# Revit family: 540_Sliding_Window_XX_Standard
name_source: partatom
category: Windows
revit_build: Autodesk Revit 2014 (Build: 20130308_1515(x64)
units: mm (PartAtom-declared; Revit-internal decimal feet)

## types (72) — shared parameters
Centered In Wall = Yes
Custom Sash Width Left = 600 mm  [stored 1.9685 ft]
Default Sill Height = 800 mm
Description = Sliding window, XX
Equal Sash Width = Yes
Frame Thickness = 54 mm  [stored 0.177165 ft]
Limit Sash Height Max = 1500 mm  [stored 4.92126 ft]
Limit Sash Height Min = 300 mm  [stored 0.984252 ft]
Limit Sash Width Max = 1200 mm
Limit Sash Width Min = 300 mm  [stored 0.984252 ft]
Limit Window Height Max = 1580 mm
Limit Window Height Min = 380 mm
Limit Window Width Max = 2418 mm
Limit Window Width Min = 618 mm
Manufacturer = Crealco
Model = 540
Rough Width = 3 mm  [stored 0.00984252 ft]
Sash Frame Seal = 3 mm  [stored 0.00984252 ft]
URL = http://www.crealco.co.za
Wall Closure = By host
zero-valued in all types: Custom Frame Offset From Exterior

## per-type parameters (varying)
- 540SW-0906XX-1000Pa: Area Left Sash Glazing=0.13 m²; Area Right Sash Glazing=0.13 m²; Clearvue SHGC Value=0.399; Clearvue U Value=7.2; Custom Windload=1000 mm  [stored 3.28084 ft]; Custom Window Height=590 mm  [stored 1.9357 ft]; Custom Window Width=890 mm  [stored 2.91995 ft]; Energy Advantage SHGC Value=0.632; Energy Advantage U Value=6.03; Heavy Duty Interlocker=No; Height=590 mm  [stored 1.9357 ft]; Intruderprufe LowE SHGC Value=0.339; Intruderprufe LowE U Value=6.19; Intruderprufe SHGC Value=0.378; Intruderprufe U Value=7.09; Is Heavy Duty Interlocker=0 mm  [stored 0 ft]; Limit Sash Width Left Max=572 mm; Limit Sash Width Left Min=300 mm  [stored 0.984252 ft]; Max Pane Area=0.13 m²; Sash Height=510 mm; Sash Width Left=436 mm; Sash Width Right=436 mm; Standard Interlocker=Yes; Width=890 mm  [stored 2.91995 ft]; Windload Design=1000 mm  [stored 3.28084 ft]
- 540SW-1206XX-1000Pa: Area Left Sash Glazing=0.19 m²; Area Right Sash Glazing=0.19 m²; Clearvue SHGC Value=0.44; Clearvue U Value=7.04; Custom Windload=1000 mm  [stored 3.28084 ft]; Custom Window Height=590 mm  [stored 1.9357 ft]; Custom Window Width=1190 mm  [stored 3.9042 ft]; Energy Advantage SHGC Value=0.397; Energy Advantage U Value=6.02; Heavy Duty Interlocker=No; Height=590 mm  [stored 1.9357 ft]; Intruderprufe LowE SHGC Value=0.372; Intruderprufe LowE U Value=5.692; Intruderprufe SHGC Value=0.416; Intruderprufe U Value=6.93; Is Heavy Duty Interlocker=0 mm  [stored 0 ft]; Limit Sash Width Left Max=872 mm; Limit Sash Width Left Min=300 mm  [stored 0.984252 ft]; Max Pane Area=0.19 m²; Sash Height=510 mm; Sash Width Left=586 mm; Sash Width Right=586 mm; Standard Interlocker=Yes; Width=1190 mm  [stored 3.9042 ft]; Windload Design=1000 mm  [stored 3.28084 ft]
- 540SW-1506XX-1000Pa: Area Left Sash Glazing=0.25 m²; Area Right Sash Glazing=0.25 m²; Clearvue SHGC Value=0.464; Clearvue U Value=6.94; Custom Windload=1000 mm  [stored 3.28084 ft]; Custom Window Height=590 mm  [stored 1.9357 ft]; Custom Window Width=1490 mm  [stored 4.88845 ft]; Energy Advantage SHGC Value=0.419; Energy Advantage U Value=5.85; Heavy Duty Interlocker=No; Height=590 mm  [stored 1.9357 ft]; Intruderprufe LowE SHGC Value=0.392; Intruderprufe LowE U Value=5.75; Intruderprufe SHGC Value=0.439; Intruderprufe U Value=6.83; Is Heavy Duty Interlocker=0 mm  [stored 0 ft]; Limit Sash Width Left Max=1172 mm; Limit Sash Width Left Min=300 mm  [stored 0.984252 ft]; Max Pane Area=0.25 m²; Sash Height=510 mm; Sash Width Left=736 mm; Sash Width Right=736 mm; Standard Interlocker=Yes; Width=1490 mm  [stored 4.88845 ft]; Windload Design=1000 mm  [stored 3.28084 ft]
- 540SW-1806XX-1000Pa: Area Left Sash Glazing=0.31 m²; Area Right Sash Glazing=0.31 m²; Clearvue SHGC Value=0.48; Clearvue U Value=6.88; Custom Windload=1000 mm  [stored 3.28084 ft]; Custom Window Height=590 mm  [stored 1.9357 ft]; Custom Window Width=1790 mm  [stored 5.8727 ft]; Energy Advantage SHGC Value=0.433; Energy Advantage U Value=5.74; Heavy Duty Interlocker=No; Height=590 mm  [stored 1.9357 ft]; Intruderprufe LowE SHGC Value=0.405; Intruderprufe LowE U Value=5.65; Intruderprufe SHGC Value=0.454; Intruderprufe U Value=6.77; Is Heavy Duty Interlocker=0 mm  [stored 0 ft]; Limit Sash Width Left Max=1200 mm; Limit Sash Width Left Min=572 mm; Max Pane Area=0.31 m²; Sash Height=510 mm; Sash Width Left=886 mm; Sash Width Right=886 mm; Standard Interlocker=Yes; Width=1790 mm  [stored 5.8727 ft]; Windload Design=1000 mm  [stored 3.28084 ft]
- 540SW-2106XX-1000Pa: Area Left Sash Glazing=0.37 m²; Area Right Sash Glazing=0.37 m²; Clearvue SHGC Value=0.492; Clearvue U Value=6.83; Custom Windload=1000 mm  [stored 3.28084 ft]; Custom Window Height=590 mm  [stored 1.9357 ft]; Custom Window Width=2090 mm  [stored 6.85696 ft]; Energy Advantage SHGC Value=0.443; Energy Advantage U Value=5.66; Heavy Duty Interlocker=No; Height=590 mm  [stored 1.9357 ft]; Intruderprufe LowE SHGC Value=0.414; Intruderprufe LowE U Value=5.57; Intruderprufe SHGC Value=0.465; Intruderprufe U Value=6.72; Is Heavy Duty Interlocker=0 mm  [stored 0 ft]; Limit Sash Width Left Max=1200 mm; Limit Sash Width Left Min=872 mm; Max Pane Area=0.37 m²; Sash Height=510 mm; Sash Width Left=1036 mm; Sash Width Right=1036 mm; Standard Interlocker=Yes; Width=2090 mm  [stored 6.85696 ft]; Windload Design=1000 mm  [stored 3.28084 ft]
- 540SW-2406XX-1000Pa: Area Left Sash Glazing=0.43 m²; Area Right Sash Glazing=0.43 m²; Clearvue SHGC Value=0.501; Clearvue U Value=6.8; Custom Windload=1000 mm  [stored 3.28084 ft]; Custom Window Height=590 mm  [stored 1.9357 ft]; Custom Window Width=2390 mm  [stored 7.84121 ft]; Energy Advantage SHGC Value=0.451; Energy Advantage U Value=5.61; Heavy Duty Interlocker=No; Height=590 mm  [stored 1.9357 ft]; Intruderprufe LowE SHGC Value=0.421; Intruderprufe LowE U Value=5.51; Intruderprufe SHGC Value=0.473; Intruderprufe U Value=6.69; Is Heavy Duty Interlocker=0 mm  [stored 0 ft]; Limit Sash Width Left Max=1200 mm; Limit Sash Width Left Min=1172 mm; Max Pane Area=0.43 m²; Sash Height=510 mm; Sash Width Left=1186 mm; Sash Width Right=1186 mm; Standard Interlocker=Yes; Width=2390 mm  [stored 7.84121 ft]; Windload Design=1000 mm  [stored 3.28084 ft]
- 540SW-0909XX-1000Pa: Area Left Sash Glazing=0.23 m²; Area Right Sash Glazing=0.23 m²; Clearvue SHGC Value=0.465; Clearvue U Value=7.31; Custom Windload=1000 mm  [stored 3.28084 ft]; Custom Window Height=890 mm  [stored 2.91995 ft]; Custom Window Width=890 mm  [stored 2.91995 ft]; Energy Advantage SHGC Value=0.42; Energy Advantage U Value=6.02; Heavy Duty Interlocker=No; Height=890 mm  [stored 2.91995 ft]; Intruderprufe LowE SHGC Value=0.392; Intruderprufe LowE U Value=5.91; Intruderprufe SHGC Value=0.439; Intruderprufe U Value=6.99; Is Heavy Duty Interlocker=0 mm  [stored 0 ft]; Limit Sash Width Left Max=572 mm; Limit Sash Width Left Min=300 mm  [stored 0.984252 ft]; Max Pane Area=0.23 m²; Sash Height=810 mm; Sash Width Left=436 mm; Sash Width Right=436 mm; Standard Interlocker=Yes; Width=890 mm  [stored 2.91995 ft]; Windload Design=1000 mm  [stored 3.28084 ft]
- 540SW-1209XX-1000Pa: Area Left Sash Glazing=0.34 m²; Area Right Sash Glazing=0.34 m²; Clearvue SHGC Value=0.513; Clearvue U Value=6.91; Custom Windload=1000 mm  [stored 3.28084 ft]; Custom Window Height=890 mm  [stored 2.91995 ft]; Custom Window Width=1190 mm  [stored 3.9042 ft]; Energy Advantage SHGC Value=0.462; Energy Advantage U Value=5.68; Heavy Duty Interlocker=No; Height=890 mm  [stored 2.91995 ft]; Intruderprufe LowE SHGC Value=0.432; Intruderprufe LowE U Value=5.59; Intruderprufe SHGC Value=0.485; Intruderprufe U Value=6.79; Is Heavy Duty Interlocker=0 mm  [stored 0 ft]; Limit Sash Width Left Max=872 mm; Limit Sash Width Left Min=300 mm  [stored 0.984252 ft]; Max Pane Area=0.34 m²; Sash Height=810 mm; Sash Width Left=586 mm; Sash Width Right=586 mm; Standard Interlocker=Yes; Width=1190 mm  [stored 3.9042 ft]; Windload Design=1000 mm  [stored 3.28084 ft]
- 540SW-1509XX-1000Pa: Area Left Sash Glazing=0.44 m²; Area Right Sash Glazing=0.44 m²; Clearvue SHGC Value=0.543; Clearvue U Value=6.79; Custom Windload=1000 mm  [stored 3.28084 ft]; Custom Window Height=890 mm  [stored 2.91995 ft]; Custom Window Width=1490 mm  [stored 4.88845 ft]; Energy Advantage SHGC Value=0.488; Energy Advantage U Value=5.48; Heavy Duty Interlocker=No; Height=890 mm  [stored 2.91995 ft]; Intruderprufe LowE SHGC Value=0.455; Intruderprufe LowE U Value=5.39; Intruderprufe SHGC Value=0.512; Intruderprufe U Value=6.68; Is Heavy Duty Interlocker=0 mm  [stored 0 ft]; Limit Sash Width Left Max=1172 mm; Limit Sash Width Left Min=300 mm  [stored 0.984252 ft]; Max Pane Area=0.44 m²; Sash Height=810 mm; Sash Width Left=736 mm; Sash Width Right=736 mm; Standard Interlocker=Yes; Width=1490 mm  [stored 4.88845 ft]; Windload Design=1000 mm  [stored 3.28084 ft]
- 540SW-1809XX-1000Pa: Area Left Sash Glazing=0.55 m²; Area Right Sash Glazing=0.55 m²; Clearvue SHGC Value=0.562; Clearvue U Value=6.71; Custom Windload=1000 mm  [stored 3.28084 ft]; Custom Window Height=890 mm  [stored 2.91995 ft]; Custom Window Width=1790 mm  [stored 5.8727 ft]; Energy Advantage SHGC Value=0.505; Energy Advantage U Value=5.35; Heavy Duty Interlocker=No; Height=890 mm  [stored 2.91995 ft]; Intruderprufe LowE SHGC Value=0.471; Intruderprufe LowE U Value=5.26; Intruderprufe SHGC Value=0.53; Intruderprufe U Value=6.6; Is Heavy Duty Interlocker=0 mm  [stored 0 ft]; Limit Sash Width Left Max=1200 mm; Limit Sash Width Left Min=572 mm; Max Pane Area=0.55 m²; Sash Height=810 mm; Sash Width Left=886 mm; Sash Width Right=886 mm; Standard Interlocker=Yes; Width=1790 mm  [stored 5.8727 ft]; Windload Design=1000 mm  [stored 3.28084 ft]
- 540SW-2109XX-1000Pa: Area Left Sash Glazing=0.65 m²; Area Right Sash Glazing=0.65 m²; Clearvue SHGC Value=0.576; Clearvue U Value=6.66; Custom Windload=1000 mm  [stored 3.28084 ft]; Custom Window Height=890 mm  [stored 2.91995 ft]; Custom Window Width=2090 mm  [stored 6.85696 ft]; Energy Advantage SHGC Value=0.517; Energy Advantage U Value=5.26; Heavy Duty Interlocker=No; Height=890 mm  [stored 2.91995 ft]; Intruderprufe LowE SHGC Value=0.482; Intruderprufe LowE U Value=5.16; Intruderprufe SHGC Value=0.543; Intruderprufe U Value=6.54; Is Heavy Duty Interlocker=0 mm  [stored 0 ft]; Limit Sash Width Left Max=1200 mm; Limit Sash Width Left Min=872 mm; Max Pane Area=0.65 m²; Sash Height=810 mm; Sash Width Left=1036 mm; Sash Width Right=1036 mm; Standard Interlocker=Yes; Width=2090 mm  [stored 6.85696 ft]; Windload Design=1000 mm  [stored 3.28084 ft]
- 540SW-2409XX-1000Pa: Area Left Sash Glazing=0.76 m²; Area Right Sash Glazing=0.76 m²; Clearvue SHGC Value=0.586; Clearvue U Value=6.62; Custom Windload=1000 mm  [stored 3.28084 ft]; Custom Window Height=890 mm  [stored 2.91995 ft]; Custom Window Width=2390 mm  [stored 7.84121 ft]; Energy Advantage SHGC Value=0.526; Energy Advantage U Value=5.19; Heavy Duty Interlocker=No; Height=890 mm  [stored 2.91995 ft]; Intruderprufe LowE SHGC Value=0.491; Intruderprufe LowE U Value=5.09; Intruderprufe SHGC Value=0.553; Intruderprufe U Value=6.5; Is Heavy Duty Interlocker=0 mm  [stored 0 ft]; Limit Sash Width Left Max=1200 mm; Limit Sash Width Left Min=1172 mm; Max Pane Area=0.76 m²; Sash Height=810 mm; Sash Width Left=1186 mm; Sash Width Right=1186 mm; Standard Interlocker=Yes; Width=2390 mm  [stored 7.84121 ft]; Windload Design=1000 mm  [stored 3.28084 ft]
- 540SW-0912XX-1000Pa: Area Left Sash Glazing=0.33 m²; Area Right Sash Glazing=0.33 m²; Clearvue SHGC Value=0.497; Clearvue U Value=7.29; Custom Windload=1000 mm  [stored 3.28084 ft]; Custom Window Height=1190 mm  [stored 3.9042 ft]; Custom Window Width=890 mm  [stored 2.91995 ft]; Energy Advantage SHGC Value=0.447; Energy Advantage U Value=6.02; Heavy Duty Interlocker=No; Height=1190 mm  [stored 3.9042 ft]; Intruderprufe LowE SHGC Value=0.419; Intruderprufe LowE U Value=5.92; Intruderprufe SHGC Value=0.47; Intruderprufe U Value=7.12; Is Heavy Duty Interlocker=0 mm  [stored 0 ft]; Limit Sash Width Left Max=572 mm; Limit Sash Width Left Min=300 mm  [stored 0.984252 ft]; Max Pane Area=0.33 m²; Sash Height=1110 mm; Sash Width Left=436 mm; Sash Width Right=436 mm; Standard Interlocker=Yes; Width=890 mm  [stored 2.91995 ft]; Windload Design=1000 mm  [stored 3.28084 ft]
- 540SW-1212XX-1000Pa: Area Left Sash Glazing=0.48 m²; Area Right Sash Glazing=0.48 m²; Clearvue SHGC Value=0.55; Clearvue U Value=6.84; Custom Windload=1000 mm  [stored 3.28084 ft]; Custom Window Height=1190 mm  [stored 3.9042 ft]; Custom Window Width=1190 mm  [stored 3.9042 ft]; Energy Advantage SHGC Value=0.495; Energy Advantage U Value=5.52; Heavy Duty Interlocker=No; Height=1190 mm  [stored 3.9042 ft]; Intruderprufe LowE SHGC Value=0.462; Intruderprufe LowE U Value=5.42; Intruderprufe SHGC Value=0.519; Intruderprufe U Value=6.73; Is Heavy Duty Interlocker=0 mm  [stored 0 ft]; Limit Sash Width Left Max=872 mm; Limit Sash Width Left Min=300 mm  [stored 0.984252 ft]; Max Pane Area=0.48 m²; Sash Height=1110 mm; Sash Width Left=586 mm; Sash Width Right=586 mm; Standard Interlocker=Yes; Width=1190 mm  [stored 3.9042 ft]; Windload Design=1000 mm  [stored 3.28084 ft]
- 540SW-1512XX-1000Pa: Area Left Sash Glazing=0.63 m²; Area Right Sash Glazing=0.63 m²; Clearvue SHGC Value=0.582; Clearvue U Value=6.72; Custom Windload=1000 mm  [stored 3.28084 ft]; Custom Window Height=1190 mm  [stored 3.9042 ft]; Custom Window Width=1490 mm  [stored 4.88845 ft]; Energy Advantage SHGC Value=0.522; Energy Advantage U Value=5.3; Heavy Duty Interlocker=No; Height=1190 mm  [stored 3.9042 ft]; Intruderprufe LowE SHGC Value=0.487; Intruderprufe LowE U Value=5.21; Intruderprufe SHGC Value=0.549; Intruderprufe U Value=6.6; Is Heavy Duty Interlocker=0 mm  [stored 0 ft]; Limit Sash Width Left Max=1172 mm; Limit Sash Width Left Min=300 mm  [stored 0.984252 ft]; Max Pane Area=0.63 m²; Sash Height=1110 mm; Sash Width Left=736 mm; Sash Width Right=736 mm; Standard Interlocker=Yes; Width=1490 mm  [stored 4.88845 ft]; Windload Design=1000 mm  [stored 3.28084 ft]
- 540SW-1812XX-1000Pa: Area Left Sash Glazing=0.78 m²; Area Right Sash Glazing=0.78 m²; Clearvue SHGC Value=0.602; Clearvue U Value=6.63; Custom Windload=1000 mm  [stored 3.28084 ft]; Custom Window Height=1190 mm  [stored 3.9042 ft]; Custom Window Width=1790 mm  [stored 5.8727 ft]; Energy Advantage SHGC Value=0.541; Energy Advantage U Value=5.16; Heavy Duty Interlocker=No; Height=1190 mm  [stored 3.9042 ft]; Intruderprufe LowE SHGC Value=0.504; Intruderprufe LowE U Value=5.07; Intruderprufe SHGC Value=0.568; Intruderprufe U Value=6.52; Is Heavy Duty Interlocker=0 mm  [stored 0 ft]; Limit Sash Width Left Max=1200 mm; Limit Sash Width Left Min=572 mm; Max Pane Area=0.78 m²; Sash Height=1110 mm; Sash Width Left=886 mm; Sash Width Right=886 mm; Standard Interlocker=Yes; Width=1790 mm  [stored 5.8727 ft]; Windload Design=1000 mm  [stored 3.28084 ft]
- 540SW-2112XX-1000Pa: Area Left Sash Glazing=0.93 m²; Area Right Sash Glazing=0.93 m²; Clearvue SHGC Value=0.617; Clearvue U Value=6.57; Custom Windload=1000 mm  [stored 3.28084 ft]; Custom Window Height=1190 mm  [stored 3.9042 ft]; Custom Window Width=2090 mm  [stored 6.85696 ft]; Energy Advantage SHGC Value=0.554; Energy Advantage U Value=5.05; Heavy Duty Interlocker=No; Height=1190 mm  [stored 3.9042 ft]; Intruderprufe LowE SHGC Value=0.516; Intruderprufe LowE U Value=4.96; Intruderprufe SHGC Value=0.582; Intruderprufe U Value=6.46; Is Heavy Duty Interlocker=0 mm  [stored 0 ft]; Limit Sash Width Left Max=1200 mm; Limit Sash Width Left Min=872 mm; Max Pane Area=0.93 m²; Sash Height=1110 mm; Sash Width Left=1036 mm; Sash Width Right=1036 mm; Standard Interlocker=Yes; Width=2090 mm  [stored 6.85696 ft]; Windload Design=1000 mm  [stored 3.28084 ft]
- 540SW-2412XX-1000Pa: Area Left Sash Glazing=1.08 m²; Area Right Sash Glazing=1.08 m²; Clearvue SHGC Value=0.629; Clearvue U Value=6.53; Custom Windload=1000 mm  [stored 3.28084 ft]; Custom Window Height=1190 mm  [stored 3.9042 ft]; Custom Window Width=2390 mm  [stored 7.84121 ft]; Energy Advantage SHGC Value=0.564; Energy Advantage U Value=4.98; Heavy Duty Interlocker=No; Height=1190 mm  [stored 3.9042 ft]; Intruderprufe LowE SHGC Value=0.525; Intruderprufe LowE U Value=4.89; Intruderprufe SHGC Value=0.593; Intruderprufe U Value=6.41; Is Heavy Duty Interlocker=0 mm  [stored 0 ft]; Limit Sash Width Left Max=1200 mm; Limit Sash Width Left Min=1172 mm; Max Pane Area=1.08 m²; Sash Height=1110 mm; Sash Width Left=1186 mm; Sash Width Right=1186 mm; Standard Interlocker=Yes; Width=2390 mm  [stored 7.84121 ft]; Windload Design=1000 mm  [stored 3.28084 ft]
- 540SW-0915XX-1000Pa: Area Left Sash Glazing=0.43 m²; Area Right Sash Glazing=0.43 m²; Clearvue SHGC Value=0.517; Clearvue U Value=7.27; Custom Windload=1000 mm  [stored 3.28084 ft]; Custom Window Height=1490 mm  [stored 4.88845 ft]; Custom Window Width=890 mm  [stored 2.91995 ft]; Energy Advantage SHGC Value=0.465; Energy Advantage U Value=5.94; Heavy Duty Interlocker=No; Height=1490 mm  [stored 4.88845 ft]; Intruderprufe LowE SHGC Value=0.435; Intruderprufe LowE U Value=5.84; Intruderprufe SHGC Value=0.448; Intruderprufe U Value=7.09; Is Heavy Duty Interlocker=0 mm  [stored 0 ft]; Limit Sash Width Left Max=572 mm; Limit Sash Width Left Min=300 mm  [stored 0.984252 ft]; Max Pane Area=0.43 m²; Sash Height=1410 mm; Sash Width Left=436 mm; Sash Width Right=436 mm; Standard Interlocker=Yes; Width=890 mm  [stored 2.91995 ft]; Windload Design=1000 mm  [stored 3.28084 ft]
- 540SW-1215XX-1000Pa: Area Left Sash Glazing=0.62 m²; Area Right Sash Glazing=0.62 m²; Clearvue SHGC Value=0.572; Clearvue U Value=6.8; Custom Windload=1000 mm  [stored 3.28084 ft]; Custom Window Height=1490 mm  [stored 4.88845 ft]; Custom Window Width=1190 mm  [stored 3.9042 ft]; Energy Advantage SHGC Value=0.514; Energy Advantage U Value=5.42; Heavy Duty Interlocker=No; Height=1490 mm  [stored 4.88845 ft]; Intruderprufe LowE SHGC Value=0.479; Intruderprufe LowE U Value=5.32; Intruderprufe SHGC Value=0.54; Intruderprufe U Value=6.69; Is Heavy Duty Interlocker=0 mm  [stored 0 ft]; Limit Sash Width Left Max=872 mm; Limit Sash Width Left Min=300 mm  [stored 0.984252 ft]; Max Pane Area=0.62 m²; Sash Height=1410 mm; Sash Width Left=586 mm; Sash Width Right=586 mm; Standard Interlocker=Yes; Width=1190 mm  [stored 3.9042 ft]; Windload Design=1000 mm  [stored 3.28084 ft]
- 540SW-1515XX-1000Pa: Area Left Sash Glazing=0.82 m²; Area Right Sash Glazing=0.82 m²; Clearvue SHGC Value=0.605; Clearvue U Value=6.67; Custom Windload=1000 mm  [stored 3.28084 ft]; Custom Window Height=1490 mm  [stored 4.88845 ft]; Custom Window Width=1490 mm  [stored 4.88845 ft]; Energy Advantage SHGC Value=0.543; Energy Advantage U Value=5.19; Heavy Duty Interlocker=Yes; Height=1490 mm  [stored 4.88845 ft]; Intruderprufe LowE SHGC Value=0.506; Intruderprufe LowE U Value=5.1; Intruderprufe SHGC Value=0.57; Intruderprufe U Value=6.55; Is Heavy Duty Interlocker=1 mm  [stored 0.00328084 ft]; Limit Sash Width Left Max=1172 mm; Limit Sash Width Left Min=300 mm  [stored 0.984252 ft]; Max Pane Area=0.82 m²; Sash Height=1410 mm; Sash Width Left=736 mm; Sash Width Right=736 mm; Standard Interlocker=No; Width=1490 mm  [stored 4.88845 ft]; Windload Design=1000 mm  [stored 3.28084 ft]
- 540SW-1815XX-1000Pa: Area Left Sash Glazing=1.01 m²; Area Right Sash Glazing=1.01 m²; Clearvue SHGC Value=0.627; Clearvue U Value=6.58; Custom Windload=1000 mm  [stored 3.28084 ft]; Custom Window Height=1490 mm  [stored 4.88845 ft]; Custom Window Width=1790 mm  [stored 5.8727 ft]; Energy Advantage SHGC Value=0.562; Energy Advantage U Value=5.04; Heavy Duty Interlocker=Yes; Height=1490 mm  [stored 4.88845 ft]; Intruderprufe LowE SHGC Value=0.524; Intruderprufe LowE U Value=4.95; Intruderprufe SHGC Value=0.591; Intruderprufe U Value=6.47; Is Heavy Duty Interlocker=1 mm  [stored 0.00328084 ft]; Limit Sash Width Left Max=1200 mm; Limit Sash Width Left Min=572 mm; Max Pane Area=1.01 m²; Sash Height=1410 mm; Sash Width Left=886 mm; Sash Width Right=886 mm; Standard Interlocker=No; Width=1790 mm  [stored 5.8727 ft]; Windload Design=1000 mm  [stored 3.28084 ft]
- 540SW-2115XX-1000Pa: Area Left Sash Glazing=1.21 m²; Area Right Sash Glazing=1.21 m²; Clearvue SHGC Value=0.642; Clearvue U Value=6.52; Custom Windload=1000 mm  [stored 3.28084 ft]; Custom Window Height=1490 mm  [stored 4.88845 ft]; Custom Window Width=2090 mm  [stored 6.85696 ft]; Energy Advantage SHGC Value=0.576; Energy Advantage U Value=4.93; Heavy Duty Interlocker=Yes; Height=1490 mm  [stored 4.88845 ft]; Intruderprufe LowE SHGC Value=0.536; Intruderprufe LowE U Value=4.84; Intruderprufe SHGC Value=0.606; Intruderprufe U Value=6.4; Is Heavy Duty Interlocker=1 mm  [stored 0.00328084 ft]; Limit Sash Width Left Max=1200 mm; Limit Sash Width Left Min=872 mm; Max Pane Area=1.21 m²; Sash Height=1410 mm; Sash Width Left=1036 mm; Sash Width Right=1036 mm; Standard Interlocker=No; Width=2090 mm  [stored 6.85696 ft]; Windload Design=1000 mm  [stored 3.28084 ft]
- 540SW-2415XX-1000Pa: Area Left Sash Glazing=1.4 m²; Area Right Sash Glazing=1.4 m²; Clearvue SHGC Value=0.654; Clearvue U Value=6.48; Custom Windload=1000 mm  [stored 3.28084 ft]; Custom Window Height=1490 mm  [stored 4.88845 ft]; Custom Window Width=2390 mm  [stored 7.84121 ft]; Energy Advantage SHGC Value=0.586; Energy Advantage U Value=4.85; Heavy Duty Interlocker=Yes; Height=1490 mm  [stored 4.88845 ft]; Intruderprufe LowE SHGC Value=0.546; Intruderprufe LowE U Value=4.77; Intruderprufe SHGC Value=0.617; Intruderprufe U Value=6.36; Is Heavy Duty Interlocker=1 mm  [stored 0.00328084 ft]; Limit Sash Width Left Max=1200 mm; Limit Sash Width Left Min=1172 mm; Max Pane Area=1.4 m²; Sash Height=1410 mm; Sash Width Left=1186 mm; Sash Width Right=1186 mm; Standard Interlocker=No; Width=2390 mm  [stored 7.84121 ft]; Windload Design=1000 mm  [stored 3.28084 ft]
- 540SW-0906XX-1500Pa: Area Left Sash Glazing=0.13 m²; Area Right Sash Glazing=0.13 m²; Clearvue SHGC Value=0.399; Clearvue U Value=7.2; Custom Windload=1500 mm  [stored 4.92126 ft]; Custom Window Height=590 mm  [stored 1.9357 ft]; Custom Window Width=890 mm  [stored 2.91995 ft]; Energy Advantage SHGC Value=0.632; Energy Advantage U Value=6.03; Heavy Duty Interlocker=No; Height=590 mm  [stored 1.9357 ft]; Intruderprufe LowE SHGC Value=0.339; Intruderprufe LowE U Value=6.19; Intruderprufe SHGC Value=0.378; Intruderprufe U Value=7.09; Is Heavy Duty Interlocker=0 mm  [stored 0 ft]; Limit Sash Width Left Max=572 mm; Limit Sash Width Left Min=300 mm  [stored 0.984252 ft]; Max Pane Area=0.13 m²; Sash Height=510 mm; Sash Width Left=436 mm; Sash Width Right=436 mm; Standard Interlocker=Yes; Width=890 mm  [stored 2.91995 ft]; Windload Design=1500 mm  [stored 4.92126 ft]
- 540SW-0906XX-2000Pa: Area Left Sash Glazing=0.13 m²; Area Right Sash Glazing=0.13 m²; Clearvue SHGC Value=0.399; Clearvue U Value=7.2; Custom Windload=2000 mm  [stored 6.56168 ft]; Custom Window Height=590 mm  [stored 1.9357 ft]; Custom Window Width=890 mm  [stored 2.91995 ft]; Energy Advantage SHGC Value=0.632; Energy Advantage U Value=6.03; Heavy Duty Interlocker=No; Height=590 mm  [stored 1.9357 ft]; Intruderprufe LowE SHGC Value=0.339; Intruderprufe LowE U Value=6.19; Intruderprufe SHGC Value=0.378; Intruderprufe U Value=7.09; Is Heavy Duty Interlocker=0 mm  [stored 0 ft]; Limit Sash Width Left Max=572 mm; Limit Sash Width Left Min=300 mm  [stored 0.984252 ft]; Max Pane Area=0.13 m²; Sash Height=510 mm; Sash Width Left=436 mm; Sash Width Right=436 mm; Standard Interlocker=Yes; Width=890 mm  [stored 2.91995 ft]; Windload Design=2000 mm  [stored 6.56168 ft]
- 540SW-0909XX-1500Pa: Area Left Sash Glazing=0.23 m²; Area Right Sash Glazing=0.23 m²; Clearvue SHGC Value=0.465; Clearvue U Value=7.31; Custom Windload=1500 mm  [stored 4.92126 ft]; Custom Window Height=890 mm  [stored 2.91995 ft]; Custom Window Width=890 mm  [stored 2.91995 ft]; Energy Advantage SHGC Value=0.42; Energy Advantage U Value=6.02; Heavy Duty Interlocker=No; Height=890 mm  [stored 2.91995 ft]; Intruderprufe LowE SHGC Value=0.392; Intruderprufe LowE U Value=5.91; Intruderprufe SHGC Value=0.439; Intruderprufe U Value=6.99; Is Heavy Duty Interlocker=0 mm  [stored 0 ft]; Limit Sash Width Left Max=572 mm; Limit Sash Width Left Min=300 mm  [stored 0.984252 ft]; Max Pane Area=0.23 m²; Sash Height=810 mm; Sash Width Left=436 mm; Sash Width Right=436 mm; Standard Interlocker=Yes; Width=890 mm  [stored 2.91995 ft]; Windload Design=1500 mm  [stored 4.92126 ft]
- 540SW-0909XX-2000Pa: Area Left Sash Glazing=0.23 m²; Area Right Sash Glazing=0.23 m²; Clearvue SHGC Value=0.465; Clearvue U Value=7.31; Custom Windload=2000 mm  [stored 6.56168 ft]; Custom Window Height=890 mm  [stored 2.91995 ft]; Custom Window Width=890 mm  [stored 2.91995 ft]; Energy Advantage SHGC Value=0.42; Energy Advantage U Value=6.02; Heavy Duty Interlocker=No; Height=890 mm  [stored 2.91995 ft]; Intruderprufe LowE SHGC Value=0.392; Intruderprufe LowE U Value=5.91; Intruderprufe SHGC Value=0.439; Intruderprufe U Value=6.99; Is Heavy Duty Interlocker=0 mm  [stored 0 ft]; Limit Sash Width Left Max=572 mm; Limit Sash Width Left Min=300 mm  [stored 0.984252 ft]; Max Pane Area=0.23 m²; Sash Height=810 mm; Sash Width Left=436 mm; Sash Width Right=436 mm; Standard Interlocker=Yes; Width=890 mm  [stored 2.91995 ft]; Windload Design=2000 mm  [stored 6.56168 ft]
- 540SW-0912XX-1500Pa: Area Left Sash Glazing=0.33 m²; Area Right Sash Glazing=0.33 m²; Clearvue SHGC Value=0.497; Clearvue U Value=7.29; Custom Windload=1500 mm  [stored 4.92126 ft]; Custom Window Height=1190 mm  [stored 3.9042 ft]; Custom Window Width=890 mm  [stored 2.91995 ft]; Energy Advantage SHGC Value=0.447; Energy Advantage U Value=6.02; Heavy Duty Interlocker=No; Height=1190 mm  [stored 3.9042 ft]; Intruderprufe LowE SHGC Value=0.419; Intruderprufe LowE U Value=5.92; Intruderprufe SHGC Value=0.47; Intruderprufe U Value=7.12; Is Heavy Duty Interlocker=0 mm  [stored 0 ft]; Limit Sash Width Left Max=572 mm; Limit Sash Width Left Min=300 mm  [stored 0.984252 ft]; Max Pane Area=0.33 m²; Sash Height=1110 mm; Sash Width Left=436 mm; Sash Width Right=436 mm; Standard Interlocker=Yes; Width=890 mm  [stored 2.91995 ft]; Windload Design=1500 mm  [stored 4.92126 ft]
- 540SW-0912XX-2000Pa: Area Left Sash Glazing=0.33 m²; Area Right Sash Glazing=0.33 m²; Clearvue SHGC Value=0.497; Clearvue U Value=7.29; Custom Windload=2000 mm  [stored 6.56168 ft]; Custom Window Height=1190 mm  [stored 3.9042 ft]; Custom Window Width=890 mm  [stored 2.91995 ft]; Energy Advantage SHGC Value=0.447; Energy Advantage U Value=6.02; Heavy Duty Interlocker=No; Height=1190 mm  [stored 3.9042 ft]; Intruderprufe LowE SHGC Value=0.419; Intruderprufe LowE U Value=5.92; Intruderprufe SHGC Value=0.47; Intruderprufe U Value=7.12; Is Heavy Duty Interlocker=0 mm  [stored 0 ft]; Limit Sash Width Left Max=572 mm; Limit Sash Width Left Min=300 mm  [stored 0.984252 ft]; Max Pane Area=0.33 m²; Sash Height=1110 mm; Sash Width Left=436 mm; Sash Width Right=436 mm; Standard Interlocker=Yes; Width=890 mm  [stored 2.91995 ft]; Windload Design=2000 mm  [stored 6.56168 ft]
- 540SW-0915XX-1500Pa: Area Left Sash Glazing=0.43 m²; Area Right Sash Glazing=0.43 m²; Clearvue SHGC Value=0.517; Clearvue U Value=7.27; Custom Windload=1500 mm  [stored 4.92126 ft]; Custom Window Height=1490 mm  [stored 4.88845 ft]; Custom Window Width=890 mm  [stored 2.91995 ft]; Energy Advantage SHGC Value=0.465; Energy Advantage U Value=5.94; Heavy Duty Interlocker=Yes; Height=1490 mm  [stored 4.88845 ft]; Intruderprufe LowE SHGC Value=0.435; Intruderprufe LowE U Value=5.84; Intruderprufe SHGC Value=0.448; Intruderprufe U Value=7.09; Is Heavy Duty Interlocker=1 mm  [stored 0.00328084 ft]; Limit Sash Width Left Max=572 mm; Limit Sash Width Left Min=300 mm  [stored 0.984252 ft]; Max Pane Area=0.43 m²; Sash Height=1410 mm; Sash Width Left=436 mm; Sash Width Right=436 mm; Standard Interlocker=No; Width=890 mm  [stored 2.91995 ft]; Windload Design=1500 mm  [stored 4.92126 ft]
- 540SW-0915XX-2000Pa: Area Left Sash Glazing=0.43 m²; Area Right Sash Glazing=0.43 m²; Clearvue SHGC Value=0.517; Clearvue U Value=7.27; Custom Windload=2000 mm  [stored 6.56168 ft]; Custom Window Height=1490 mm  [stored 4.88845 ft]; Custom Window Width=890 mm  [stored 2.91995 ft]; Energy Advantage SHGC Value=0.465; Energy Advantage U Value=5.94; Heavy Duty Interlocker=Yes; Height=1490 mm  [stored 4.88845 ft]; Intruderprufe LowE SHGC Value=0.435; Intruderprufe LowE U Value=5.84; Intruderprufe SHGC Value=0.448; Intruderprufe U Value=7.09; Is Heavy Duty Interlocker=1 mm  [stored 0.00328084 ft]; Limit Sash Width Left Max=572 mm; Limit Sash Width Left Min=300 mm  [stored 0.984252 ft]; Max Pane Area=0.43 m²; Sash Height=1410 mm; Sash Width Left=436 mm; Sash Width Right=436 mm; Standard Interlocker=No; Width=890 mm  [stored 2.91995 ft]; Windload Design=2000 mm  [stored 6.56168 ft]
- 540SW-1206XX-1500Pa: Area Left Sash Glazing=0.19 m²; Area Right Sash Glazing=0.19 m²; Clearvue SHGC Value=0.44; Clearvue U Value=7.04; Custom Windload=1500 mm  [stored 4.92126 ft]; Custom Window Height=590 mm  [stored 1.9357 ft]; Custom Window Width=1190 mm  [stored 3.9042 ft]; Energy Advantage SHGC Value=0.397; Energy Advantage U Value=6.02; Heavy Duty Interlocker=No; Height=590 mm  [stored 1.9357 ft]; Intruderprufe LowE SHGC Value=0.372; Intruderprufe LowE U Value=5.692; Intruderprufe SHGC Value=0.416; Intruderprufe U Value=6.93; Is Heavy Duty Interlocker=0 mm  [stored 0 ft]; Limit Sash Width Left Max=872 mm; Limit Sash Width Left Min=300 mm  [stored 0.984252 ft]; Max Pane Area=0.19 m²; Sash Height=510 mm; Sash Width Left=586 mm; Sash Width Right=586 mm; Standard Interlocker=Yes; Width=1190 mm  [stored 3.9042 ft]; Windload Design=1500 mm  [stored 4.92126 ft]
- 540SW-1206XX-2000Pa: Area Left Sash Glazing=0.19 m²; Area Right Sash Glazing=0.19 m²; Clearvue SHGC Value=0.44; Clearvue U Value=7.04; Custom Windload=2000 mm  [stored 6.56168 ft]; Custom Window Height=590 mm  [stored 1.9357 ft]; Custom Window Width=1190 mm  [stored 3.9042 ft]; Energy Advantage SHGC Value=0.397; Energy Advantage U Value=6.02; Heavy Duty Interlocker=No; Height=590 mm  [stored 1.9357 ft]; Intruderprufe LowE SHGC Value=0.372; Intruderprufe LowE U Value=5.692; Intruderprufe SHGC Value=0.416; Intruderprufe U Value=6.93; Is Heavy Duty Interlocker=0 mm  [stored 0 ft]; Limit Sash Width Left Max=872 mm; Limit Sash Width Left Min=300 mm  [stored 0.984252 ft]; Max Pane Area=0.19 m²; Sash Height=510 mm; Sash Width Left=586 mm; Sash Width Right=586 mm; Standard Interlocker=Yes; Width=1190 mm  [stored 3.9042 ft]; Windload Design=2000 mm  [stored 6.56168 ft]
- 540SW-1209XX-1500Pa: Area Left Sash Glazing=0.34 m²; Area Right Sash Glazing=0.34 m²; Clearvue SHGC Value=0.513; Clearvue U Value=6.91; Custom Windload=1500 mm  [stored 4.92126 ft]; Custom Window Height=890 mm  [stored 2.91995 ft]; Custom Window Width=1190 mm  [stored 3.9042 ft]; Energy Advantage SHGC Value=0.462; Energy Advantage U Value=5.68; Heavy Duty Interlocker=No; Height=890 mm  [stored 2.91995 ft]; Intruderprufe LowE SHGC Value=0.432; Intruderprufe LowE U Value=5.59; Intruderprufe SHGC Value=0.485; Intruderprufe U Value=6.79; Is Heavy Duty Interlocker=0 mm  [stored 0 ft]; Limit Sash Width Left Max=872 mm; Limit Sash Width Left Min=300 mm  [stored 0.984252 ft]; Max Pane Area=0.34 m²; Sash Height=810 mm; Sash Width Left=586 mm; Sash Width Right=586 mm; Standard Interlocker=Yes; Width=1190 mm  [stored 3.9042 ft]; Windload Design=1500 mm  [stored 4.92126 ft]
- 540SW-1209XX-2000Pa: Area Left Sash Glazing=0.34 m²; Area Right Sash Glazing=0.34 m²; Clearvue SHGC Value=0.513; Clearvue U Value=6.91; Custom Windload=2000 mm  [stored 6.56168 ft]; Custom Window Height=890 mm  [stored 2.91995 ft]; Custom Window Width=1190 mm  [stored 3.9042 ft]; Energy Advantage SHGC Value=0.462; Energy Advantage U Value=5.68; Heavy Duty Interlocker=No; Height=890 mm  [stored 2.91995 ft]; Intruderprufe LowE SHGC Value=0.432; Intruderprufe LowE U Value=5.59; Intruderprufe SHGC Value=0.485; Intruderprufe U Value=6.79; Is Heavy Duty Interlocker=0 mm  [stored 0 ft]; Limit Sash Width Left Max=872 mm; Limit Sash Width Left Min=300 mm  [stored 0.984252 ft]; Max Pane Area=0.34 m²; Sash Height=810 mm; Sash Width Left=586 mm; Sash Width Right=586 mm; Standard Interlocker=Yes; Width=1190 mm  [stored 3.9042 ft]; Windload Design=2000 mm  [stored 6.56168 ft]
- 540SW-1212XX-1500Pa: Area Left Sash Glazing=0.48 m²; Area Right Sash Glazing=0.48 m²; Clearvue SHGC Value=0.55; Clearvue U Value=6.84; Custom Windload=1500 mm  [stored 4.92126 ft]; Custom Window Height=1190 mm  [stored 3.9042 ft]; Custom Window Width=1190 mm  [stored 3.9042 ft]; Energy Advantage SHGC Value=0.495; Energy Advantage U Value=5.52; Heavy Duty Interlocker=No; Height=1190 mm  [stored 3.9042 ft]; Intruderprufe LowE SHGC Value=0.462; Intruderprufe LowE U Value=5.42; Intruderprufe SHGC Value=0.519; Intruderprufe U Value=6.73; Is Heavy Duty Interlocker=0 mm  [stored 0 ft]; Limit Sash Width Left Max=872 mm; Limit Sash Width Left Min=300 mm  [stored 0.984252 ft]; Max Pane Area=0.48 m²; Sash Height=1110 mm; Sash Width Left=586 mm; Sash Width Right=586 mm; Standard Interlocker=Yes; Width=1190 mm  [stored 3.9042 ft]; Windload Design=1500 mm  [stored 4.92126 ft]
- 540SW-1212XX-2000Pa: Area Left Sash Glazing=0.48 m²; Area Right Sash Glazing=0.48 m²; Clearvue SHGC Value=0.55; Clearvue U Value=6.84; Custom Windload=2000 mm  [stored 6.56168 ft]; Custom Window Height=1190 mm  [stored 3.9042 ft]; Custom Window Width=1190 mm  [stored 3.9042 ft]; Energy Advantage SHGC Value=0.495; Energy Advantage U Value=5.52; Heavy Duty Interlocker=No; Height=1190 mm  [stored 3.9042 ft]; Intruderprufe LowE SHGC Value=0.462; Intruderprufe LowE U Value=5.42; Intruderprufe SHGC Value=0.519; Intruderprufe U Value=6.73; Is Heavy Duty Interlocker=0 mm  [stored 0 ft]; Limit Sash Width Left Max=872 mm; Limit Sash Width Left Min=300 mm  [stored 0.984252 ft]; Max Pane Area=0.48 m²; Sash Height=1110 mm; Sash Width Left=586 mm; Sash Width Right=586 mm; Standard Interlocker=Yes; Width=1190 mm  [stored 3.9042 ft]; Windload Design=2000 mm  [stored 6.56168 ft]
- 540SW-1215XX-1500Pa: Area Left Sash Glazing=0.62 m²; Area Right Sash Glazing=0.62 m²; Clearvue SHGC Value=0.572; Clearvue U Value=6.8; Custom Windload=1500 mm  [stored 4.92126 ft]; Custom Window Height=1490 mm  [stored 4.88845 ft]; Custom Window Width=1190 mm  [stored 3.9042 ft]; Energy Advantage SHGC Value=0.514; Energy Advantage U Value=5.42; Heavy Duty Interlocker=Yes; Height=1490 mm  [stored 4.88845 ft]; Intruderprufe LowE SHGC Value=0.479; Intruderprufe LowE U Value=5.32; Intruderprufe SHGC Value=0.54; Intruderprufe U Value=6.69; Is Heavy Duty Interlocker=1 mm  [stored 0.00328084 ft]; Limit Sash Width Left Max=872 mm; Limit Sash Width Left Min=300 mm  [stored 0.984252 ft]; Max Pane Area=0.62 m²; Sash Height=1410 mm; Sash Width Left=586 mm; Sash Width Right=586 mm; Standard Interlocker=No; Width=1190 mm  [stored 3.9042 ft]; Windload Design=1500 mm  [stored 4.92126 ft]
- 540SW-1215XX-2000Pa: Area Left Sash Glazing=0.62 m²; Area Right Sash Glazing=0.62 m²; Clearvue SHGC Value=0.572; Clearvue U Value=6.8; Custom Windload=2000 mm  [stored 6.56168 ft]; Custom Window Height=1490 mm  [stored 4.88845 ft]; Custom Window Width=1190 mm  [stored 3.9042 ft]; Energy Advantage SHGC Value=0.514; Energy Advantage U Value=5.42; Heavy Duty Interlocker=Yes; Height=1490 mm  [stored 4.88845 ft]; Intruderprufe LowE SHGC Value=0.479; Intruderprufe LowE U Value=5.32; Intruderprufe SHGC Value=0.54; Intruderprufe U Value=6.69; Is Heavy Duty Interlocker=1 mm  [stored 0.00328084 ft]; Limit Sash Width Left Max=872 mm; Limit Sash Width Left Min=300 mm  [stored 0.984252 ft]; Max Pane Area=0.62 m²; Sash Height=1410 mm; Sash Width Left=586 mm; Sash Width Right=586 mm; Standard Interlocker=No; Width=1190 mm  [stored 3.9042 ft]; Windload Design=2000 mm  [stored 6.56168 ft]
- 540SW-1506XX-1500Pa: Area Left Sash Glazing=0.25 m²; Area Right Sash Glazing=0.25 m²; Clearvue SHGC Value=0.464; Clearvue U Value=6.94; Custom Windload=1500 mm  [stored 4.92126 ft]; Custom Window Height=590 mm  [stored 1.9357 ft]; Custom Window Width=1490 mm  [stored 4.88845 ft]; Energy Advantage SHGC Value=0.419; Energy Advantage U Value=5.85; Heavy Duty Interlocker=No; Height=590 mm  [stored 1.9357 ft]; Intruderprufe LowE SHGC Value=0.392; Intruderprufe LowE U Value=5.75; Intruderprufe SHGC Value=0.439; Intruderprufe U Value=6.83; Is Heavy Duty Interlocker=0 mm  [stored 0 ft]; Limit Sash Width Left Max=1172 mm; Limit Sash Width Left Min=300 mm  [stored 0.984252 ft]; Max Pane Area=0.25 m²; Sash Height=510 mm; Sash Width Left=736 mm; Sash Width Right=736 mm; Standard Interlocker=Yes; Width=1490 mm  [stored 4.88845 ft]; Windload Design=1500 mm  [stored 4.92126 ft]
- 540SW-1506XX-2000Pa: Area Left Sash Glazing=0.25 m²; Area Right Sash Glazing=0.25 m²; Clearvue SHGC Value=0.464; Clearvue U Value=6.94; Custom Windload=2000 mm  [stored 6.56168 ft]; Custom Window Height=590 mm  [stored 1.9357 ft]; Custom Window Width=1490 mm  [stored 4.88845 ft]; Energy Advantage SHGC Value=0.419; Energy Advantage U Value=5.85; Heavy Duty Interlocker=No; Height=590 mm  [stored 1.9357 ft]; Intruderprufe LowE SHGC Value=0.392; Intruderprufe LowE U Value=5.75; Intruderprufe SHGC Value=0.439; Intruderprufe U Value=6.83; Is Heavy Duty Interlocker=0 mm  [stored 0 ft]; Limit Sash Width Left Max=1172 mm; Limit Sash Width Left Min=300 mm  [stored 0.984252 ft]; Max Pane Area=0.25 m²; Sash Height=510 mm; Sash Width Left=736 mm; Sash Width Right=736 mm; Standard Interlocker=Yes; Width=1490 mm  [stored 4.88845 ft]; Windload Design=2000 mm  [stored 6.56168 ft]
- 540SW-1509XX-1500Pa: Area Left Sash Glazing=0.44 m²; Area Right Sash Glazing=0.44 m²; Clearvue SHGC Value=0.543; Clearvue U Value=6.79; Custom Windload=1500 mm  [stored 4.92126 ft]; Custom Window Height=890 mm  [stored 2.91995 ft]; Custom Window Width=1490 mm  [stored 4.88845 ft]; Energy Advantage SHGC Value=0.488; Energy Advantage U Value=5.48; Heavy Duty Interlocker=No; Height=890 mm  [stored 2.91995 ft]; Intruderprufe LowE SHGC Value=0.455; Intruderprufe LowE U Value=5.39; Intruderprufe SHGC Value=0.512; Intruderprufe U Value=6.68; Is Heavy Duty Interlocker=0 mm  [stored 0 ft]; Limit Sash Width Left Max=1172 mm; Limit Sash Width Left Min=300 mm  [stored 0.984252 ft]; Max Pane Area=0.44 m²; Sash Height=810 mm; Sash Width Left=736 mm; Sash Width Right=736 mm; Standard Interlocker=Yes; Width=1490 mm  [stored 4.88845 ft]; Windload Design=1500 mm  [stored 4.92126 ft]
- 540SW-1509XX-2000Pa: Area Left Sash Glazing=0.44 m²; Area Right Sash Glazing=0.44 m²; Clearvue SHGC Value=0.543; Clearvue U Value=6.79; Custom Windload=2000 mm  [stored 6.56168 ft]; Custom Window Height=890 mm  [stored 2.91995 ft]; Custom Window Width=1490 mm  [stored 4.88845 ft]; Energy Advantage SHGC Value=0.488; Energy Advantage U Value=5.48; Heavy Duty Interlocker=No; Height=890 mm  [stored 2.91995 ft]; Intruderprufe LowE SHGC Value=0.455; Intruderprufe LowE U Value=5.39; Intruderprufe SHGC Value=0.512; Intruderprufe U Value=6.68; Is Heavy Duty Interlocker=0 mm  [stored 0 ft]; Limit Sash Width Left Max=1172 mm; Limit Sash Width Left Min=300 mm  [stored 0.984252 ft]; Max Pane Area=0.44 m²; Sash Height=810 mm; Sash Width Left=736 mm; Sash Width Right=736 mm; Standard Interlocker=Yes; Width=1490 mm  [stored 4.88845 ft]; Windload Design=2000 mm  [stored 6.56168 ft]
- 540SW-1512XX-1500Pa: Area Left Sash Glazing=0.63 m²; Area Right Sash Glazing=0.63 m²; Clearvue SHGC Value=0.582; Clearvue U Value=6.72; Custom Windload=1500 mm  [stored 4.92126 ft]; Custom Window Height=1190 mm  [stored 3.9042 ft]; Custom Window Width=1490 mm  [stored 4.88845 ft]; Energy Advantage SHGC Value=0.522; Energy Advantage U Value=5.3; Heavy Duty Interlocker=No; Height=1190 mm  [stored 3.9042 ft]; Intruderprufe LowE SHGC Value=0.487; Intruderprufe LowE U Value=5.21; Intruderprufe SHGC Value=0.549; Intruderprufe U Value=6.6; Is Heavy Duty Interlocker=0 mm  [stored 0 ft]; Limit Sash Width Left Max=1172 mm; Limit Sash Width Left Min=300 mm  [stored 0.984252 ft]; Max Pane Area=0.63 m²; Sash Height=1110 mm; Sash Width Left=736 mm; Sash Width Right=736 mm; Standard Interlocker=Yes; Width=1490 mm  [stored 4.88845 ft]; Windload Design=1500 mm  [stored 4.92126 ft]
- 540SW-1512XX-2000Pa: Area Left Sash Glazing=0.63 m²; Area Right Sash Glazing=0.63 m²; Clearvue SHGC Value=0.582; Clearvue U Value=6.72; Custom Windload=2000 mm  [stored 6.56168 ft]; Custom Window Height=1190 mm  [stored 3.9042 ft]; Custom Window Width=1490 mm  [stored 4.88845 ft]; Energy Advantage SHGC Value=0.522; Energy Advantage U Value=5.3; Heavy Duty Interlocker=Yes; Height=1190 mm  [stored 3.9042 ft]; Intruderprufe LowE SHGC Value=0.487; Intruderprufe LowE U Value=5.21; Intruderprufe SHGC Value=0.549; Intruderprufe U Value=6.6; Is Heavy Duty Interlocker=1 mm  [stored 0.00328084 ft]; Limit Sash Width Left Max=1172 mm; Limit Sash Width Left Min=300 mm  [stored 0.984252 ft]; Max Pane Area=0.63 m²; Sash Height=1110 mm; Sash Width Left=736 mm; Sash Width Right=736 mm; Standard Interlocker=No; Width=1490 mm  [stored 4.88845 ft]; Windload Design=2000 mm  [stored 6.56168 ft]
- 540SW-1515XX-1500Pa: Area Left Sash Glazing=0.82 m²; Area Right Sash Glazing=0.82 m²; Clearvue SHGC Value=0.605; Clearvue U Value=6.67; Custom Windload=1500 mm  [stored 4.92126 ft]; Custom Window Height=1490 mm  [stored 4.88845 ft]; Custom Window Width=1490 mm  [stored 4.88845 ft]; Energy Advantage SHGC Value=0.543; Energy Advantage U Value=5.19; Heavy Duty Interlocker=Yes; Height=1490 mm  [stored 4.88845 ft]; Intruderprufe LowE SHGC Value=0.506; Intruderprufe LowE U Value=5.1; Intruderprufe SHGC Value=0.57; Intruderprufe U Value=6.55; Is Heavy Duty Interlocker=1 mm  [stored 0.00328084 ft]; Limit Sash Width Left Max=1172 mm; Limit Sash Width Left Min=300 mm  [stored 0.984252 ft]; Max Pane Area=0.82 m²; Sash Height=1410 mm; Sash Width Left=736 mm; Sash Width Right=736 mm; Standard Interlocker=No; Width=1490 mm  [stored 4.88845 ft]; Windload Design=1500 mm  [stored 4.92126 ft]
- 540SW-1515XX-2000Pa: Area Left Sash Glazing=0.82 m²; Area Right Sash Glazing=0.82 m²; Clearvue SHGC Value=0.605; Clearvue U Value=6.67; Custom Windload=2000 mm  [stored 6.56168 ft]; Custom Window Height=1490 mm  [stored 4.88845 ft]; Custom Window Width=1490 mm  [stored 4.88845 ft]; Energy Advantage SHGC Value=0.543; Energy Advantage U Value=5.19; Heavy Duty Interlocker=Yes; Height=1490 mm  [stored 4.88845 ft]; Intruderprufe LowE SHGC Value=0.506; Intruderprufe LowE U Value=5.1; Intruderprufe SHGC Value=0.57; Intruderprufe U Value=6.55; Is Heavy Duty Interlocker=1 mm  [stored 0.00328084 ft]; Limit Sash Width Left Max=1172 mm; Limit Sash Width Left Min=300 mm  [stored 0.984252 ft]; Max Pane Area=0.82 m²; Sash Height=1410 mm; Sash Width Left=736 mm; Sash Width Right=736 mm; Standard Interlocker=No; Width=1490 mm  [stored 4.88845 ft]; Windload Design=2000 mm  [stored 6.56168 ft]
- 540SW-1806XX-1500Pa: Area Left Sash Glazing=0.31 m²; Area Right Sash Glazing=0.31 m²; Clearvue SHGC Value=0.48; Clearvue U Value=6.88; Custom Windload=1500 mm  [stored 4.92126 ft]; Custom Window Height=590 mm  [stored 1.9357 ft]; Custom Window Width=1790 mm  [stored 5.8727 ft]; Energy Advantage SHGC Value=0.433; Energy Advantage U Value=5.74; Heavy Duty Interlocker=No; Height=590 mm  [stored 1.9357 ft]; Intruderprufe LowE SHGC Value=0.405; Intruderprufe LowE U Value=5.65; Intruderprufe SHGC Value=0.454; Intruderprufe U Value=6.77; Is Heavy Duty Interlocker=0 mm  [stored 0 ft]; Limit Sash Width Left Max=1200 mm; Limit Sash Width Left Min=572 mm; Max Pane Area=0.31 m²; Sash Height=510 mm; Sash Width Left=886 mm; Sash Width Right=886 mm; Standard Interlocker=Yes; Width=1790 mm  [stored 5.8727 ft]; Windload Design=1500 mm  [stored 4.92126 ft]
- 540SW-1806XX-2000Pa: Area Left Sash Glazing=0.31 m²; Area Right Sash Glazing=0.31 m²; Clearvue SHGC Value=0.48; Clearvue U Value=6.88; Custom Windload=2000 mm  [stored 6.56168 ft]; Custom Window Height=590 mm  [stored 1.9357 ft]; Custom Window Width=1790 mm  [stored 5.8727 ft]; Energy Advantage SHGC Value=0.433; Energy Advantage U Value=5.74; Heavy Duty Interlocker=No; Height=590 mm  [stored 1.9357 ft]; Intruderprufe LowE SHGC Value=0.405; Intruderprufe LowE U Value=5.65; Intruderprufe SHGC Value=0.454; Intruderprufe U Value=6.77; Is Heavy Duty Interlocker=0 mm  [stored 0 ft]; Limit Sash Width Left Max=1200 mm; Limit Sash Width Left Min=572 mm; Max Pane Area=0.31 m²; Sash Height=510 mm; Sash Width Left=886 mm; Sash Width Right=886 mm; Standard Interlocker=Yes; Width=1790 mm  [stored 5.8727 ft]; Windload Design=2000 mm  [stored 6.56168 ft]
- 540SW-1809XX-1500Pa: Area Left Sash Glazing=0.55 m²; Area Right Sash Glazing=0.55 m²; Clearvue SHGC Value=0.562; Clearvue U Value=6.71; Custom Windload=1500 mm  [stored 4.92126 ft]; Custom Window Height=890 mm  [stored 2.91995 ft]; Custom Window Width=1790 mm  [stored 5.8727 ft]; Energy Advantage SHGC Value=0.505; Energy Advantage U Value=5.35; Heavy Duty Interlocker=No; Height=890 mm  [stored 2.91995 ft]; Intruderprufe LowE SHGC Value=0.471; Intruderprufe LowE U Value=5.26; Intruderprufe SHGC Value=0.53; Intruderprufe U Value=6.6; Is Heavy Duty Interlocker=0 mm  [stored 0 ft]; Limit Sash Width Left Max=1200 mm; Limit Sash Width Left Min=572 mm; Max Pane Area=0.55 m²; Sash Height=810 mm; Sash Width Left=886 mm; Sash Width Right=886 mm; Standard Interlocker=Yes; Width=1790 mm  [stored 5.8727 ft]; Windload Design=1500 mm  [stored 4.92126 ft]
- 540SW-1809XX-2000Pa: Area Left Sash Glazing=0.55 m²; Area Right Sash Glazing=0.55 m²; Clearvue SHGC Value=0.562; Clearvue U Value=6.71; Custom Windload=2000 mm  [stored 6.56168 ft]; Custom Window Height=890 mm  [stored 2.91995 ft]; Custom Window Width=1790 mm  [stored 5.8727 ft]; Energy Advantage SHGC Value=0.505; Energy Advantage U Value=5.35; Heavy Duty Interlocker=No; Height=890 mm  [stored 2.91995 ft]; Intruderprufe LowE SHGC Value=0.471; Intruderprufe LowE U Value=5.26; Intruderprufe SHGC Value=0.53; Intruderprufe U Value=6.6; Is Heavy Duty Interlocker=0 mm  [stored 0 ft]; Limit Sash Width Left Max=1200 mm; Limit Sash Width Left Min=572 mm; Max Pane Area=0.55 m²; Sash Height=810 mm; Sash Width Left=886 mm; Sash Width Right=886 mm; Standard Interlocker=Yes; Width=1790 mm  [stored 5.8727 ft]; Windload Design=2000 mm  [stored 6.56168 ft]
- 540SW-1812XX-1500Pa: Area Left Sash Glazing=0.78 m²; Area Right Sash Glazing=0.78 m²; Clearvue SHGC Value=0.602; Clearvue U Value=6.63; Custom Windload=1500 mm  [stored 4.92126 ft]; Custom Window Height=1190 mm  [stored 3.9042 ft]; Custom Window Width=1790 mm  [stored 5.8727 ft]; Energy Advantage SHGC Value=0.541; Energy Advantage U Value=5.16; Heavy Duty Interlocker=No; Height=1190 mm  [stored 3.9042 ft]; Intruderprufe LowE SHGC Value=0.504; Intruderprufe LowE U Value=5.07; Intruderprufe SHGC Value=0.568; Intruderprufe U Value=6.52; Is Heavy Duty Interlocker=0 mm  [stored 0 ft]; Limit Sash Width Left Max=1200 mm; Limit Sash Width Left Min=572 mm; Max Pane Area=0.78 m²; Sash Height=1110 mm; Sash Width Left=886 mm; Sash Width Right=886 mm; Standard Interlocker=Yes; Width=1790 mm  [stored 5.8727 ft]; Windload Design=1500 mm  [stored 4.92126 ft]
- 540SW-1812XX-2000Pa: Area Left Sash Glazing=0.78 m²; Area Right Sash Glazing=0.78 m²; Clearvue SHGC Value=0.602; Clearvue U Value=6.63; Custom Windload=2000 mm  [stored 6.56168 ft]; Custom Window Height=1190 mm  [stored 3.9042 ft]; Custom Window Width=1790 mm  [stored 5.8727 ft]; Energy Advantage SHGC Value=0.541; Energy Advantage U Value=5.16; Heavy Duty Interlocker=Yes; Height=1190 mm  [stored 3.9042 ft]; Intruderprufe LowE SHGC Value=0.504; Intruderprufe LowE U Value=5.07; Intruderprufe SHGC Value=0.568; Intruderprufe U Value=6.52; Is Heavy Duty Interlocker=1 mm  [stored 0.00328084 ft]; Limit Sash Width Left Max=1200 mm; Limit Sash Width Left Min=572 mm; Max Pane Area=0.78 m²; Sash Height=1110 mm; Sash Width Left=886 mm; Sash Width Right=886 mm; Standard Interlocker=No; Width=1790 mm  [stored 5.8727 ft]; Windload Design=2000 mm  [stored 6.56168 ft]
- 540SW-1815XX-1500Pa: Area Left Sash Glazing=1.01 m²; Area Right Sash Glazing=1.01 m²; Clearvue SHGC Value=0.627; Clearvue U Value=6.58; Custom Windload=1500 mm  [stored 4.92126 ft]; Custom Window Height=1490 mm  [stored 4.88845 ft]; Custom Window Width=1790 mm  [stored 5.8727 ft]; Energy Advantage SHGC Value=0.562; Energy Advantage U Value=5.04; Heavy Duty Interlocker=Yes; Height=1490 mm  [stored 4.88845 ft]; Intruderprufe LowE SHGC Value=0.524; Intruderprufe LowE U Value=4.95; Intruderprufe SHGC Value=0.591; Intruderprufe U Value=6.47; Is Heavy Duty Interlocker=1 mm  [stored 0.00328084 ft]; Limit Sash Width Left Max=1200 mm; Limit Sash Width Left Min=572 mm; Max Pane Area=1.01 m²; Sash Height=1410 mm; Sash Width Left=886 mm; Sash Width Right=886 mm; Standard Interlocker=No; Width=1790 mm  [stored 5.8727 ft]; Windload Design=1500 mm  [stored 4.92126 ft]
- 540SW-1815XX-2000Pa: Area Left Sash Glazing=1.01 m²; Area Right Sash Glazing=1.01 m²; Clearvue SHGC Value=0.627; Clearvue U Value=6.58; Custom Windload=2000 mm  [stored 6.56168 ft]; Custom Window Height=1490 mm  [stored 4.88845 ft]; Custom Window Width=1790 mm  [stored 5.8727 ft]; Energy Advantage SHGC Value=0.562; Energy Advantage U Value=5.04; Heavy Duty Interlocker=Yes; Height=1490 mm  [stored 4.88845 ft]; Intruderprufe LowE SHGC Value=0.524; Intruderprufe LowE U Value=4.95; Intruderprufe SHGC Value=0.591; Intruderprufe U Value=6.47; Is Heavy Duty Interlocker=1 mm  [stored 0.00328084 ft]; Limit Sash Width Left Max=1200 mm; Limit Sash Width Left Min=572 mm; Max Pane Area=1.01 m²; Sash Height=1410 mm; Sash Width Left=886 mm; Sash Width Right=886 mm; Standard Interlocker=No; Width=1790 mm  [stored 5.8727 ft]; Windload Design=2000 mm  [stored 6.56168 ft]
- 540SW-2106XX-1500Pa: Area Left Sash Glazing=0.37 m²; Area Right Sash Glazing=0.37 m²; Clearvue SHGC Value=0.492; Clearvue U Value=6.83; Custom Windload=1500 mm  [stored 4.92126 ft]; Custom Window Height=590 mm  [stored 1.9357 ft]; Custom Window Width=2090 mm  [stored 6.85696 ft]; Energy Advantage SHGC Value=0.443; Energy Advantage U Value=5.66; Heavy Duty Interlocker=No; Height=590 mm  [stored 1.9357 ft]; Intruderprufe LowE SHGC Value=0.414; Intruderprufe LowE U Value=5.57; Intruderprufe SHGC Value=0.465; Intruderprufe U Value=6.72; Is Heavy Duty Interlocker=0 mm  [stored 0 ft]; Limit Sash Width Left Max=1200 mm; Limit Sash Width Left Min=872 mm; Max Pane Area=0.37 m²; Sash Height=510 mm; Sash Width Left=1036 mm; Sash Width Right=1036 mm; Standard Interlocker=Yes; Width=2090 mm  [stored 6.85696 ft]; Windload Design=1500 mm  [stored 4.92126 ft]
- 540SW-2106XX-2000Pa: Area Left Sash Glazing=0.37 m²; Area Right Sash Glazing=0.37 m²; Clearvue SHGC Value=0.492; Clearvue U Value=6.83; Custom Windload=2000 mm  [stored 6.56168 ft]; Custom Window Height=590 mm  [stored 1.9357 ft]; Custom Window Width=2090 mm  [stored 6.85696 ft]; Energy Advantage SHGC Value=0.443; Energy Advantage U Value=5.66; Heavy Duty Interlocker=No; Height=590 mm  [stored 1.9357 ft]; Intruderprufe LowE SHGC Value=0.414; Intruderprufe LowE U Value=5.57; Intruderprufe SHGC Value=0.465; Intruderprufe U Value=6.72; Is Heavy Duty Interlocker=0 mm  [stored 0 ft]; Limit Sash Width Left Max=1200 mm; Limit Sash Width Left Min=872 mm; Max Pane Area=0.37 m²; Sash Height=510 mm; Sash Width Left=1036 mm; Sash Width Right=1036 mm; Standard Interlocker=Yes; Width=2090 mm  [stored 6.85696 ft]; Windload Design=2000 mm  [stored 6.56168 ft]
- 540SW-2109XX-1500Pa: Area Left Sash Glazing=0.65 m²; Area Right Sash Glazing=0.65 m²; Clearvue SHGC Value=0.576; Clearvue U Value=6.66; Custom Windload=1500 mm  [stored 4.92126 ft]; Custom Window Height=890 mm  [stored 2.91995 ft]; Custom Window Width=2090 mm  [stored 6.85696 ft]; Energy Advantage SHGC Value=0.517; Energy Advantage U Value=5.26; Heavy Duty Interlocker=No; Height=890 mm  [stored 2.91995 ft]; Intruderprufe LowE SHGC Value=0.482; Intruderprufe LowE U Value=5.16; Intruderprufe SHGC Value=0.543; Intruderprufe U Value=6.54; Is Heavy Duty Interlocker=0 mm  [stored 0 ft]; Limit Sash Width Left Max=1200 mm; Limit Sash Width Left Min=872 mm; Max Pane Area=0.65 m²; Sash Height=810 mm; Sash Width Left=1036 mm; Sash Width Right=1036 mm; Standard Interlocker=Yes; Width=2090 mm  [stored 6.85696 ft]; Windload Design=1500 mm  [stored 4.92126 ft]
- 540SW-2109XX-2000Pa: Area Left Sash Glazing=0.65 m²; Area Right Sash Glazing=0.65 m²; Clearvue SHGC Value=0.576; Clearvue U Value=6.66; Custom Windload=2000 mm  [stored 6.56168 ft]; Custom Window Height=890 mm  [stored 2.91995 ft]; Custom Window Width=2090 mm  [stored 6.85696 ft]; Energy Advantage SHGC Value=0.517; Energy Advantage U Value=5.26; Heavy Duty Interlocker=No; Height=890 mm  [stored 2.91995 ft]; Intruderprufe LowE SHGC Value=0.482; Intruderprufe LowE U Value=5.16; Intruderprufe SHGC Value=0.543; Intruderprufe U Value=6.54; Is Heavy Duty Interlocker=0 mm  [stored 0 ft]; Limit Sash Width Left Max=1200 mm; Limit Sash Width Left Min=872 mm; Max Pane Area=0.65 m²; Sash Height=810 mm; Sash Width Left=1036 mm; Sash Width Right=1036 mm; Standard Interlocker=Yes; Width=2090 mm  [stored 6.85696 ft]; Windload Design=2000 mm  [stored 6.56168 ft]
- 540SW-2112XX-1500Pa: Area Left Sash Glazing=0.93 m²; Area Right Sash Glazing=0.93 m²; Clearvue SHGC Value=0.617; Clearvue U Value=6.57; Custom Windload=1500 mm  [stored 4.92126 ft]; Custom Window Height=1190 mm  [stored 3.9042 ft]; Custom Window Width=2090 mm  [stored 6.85696 ft]; Energy Advantage SHGC Value=0.554; Energy Advantage U Value=5.05; Heavy Duty Interlocker=No; Height=1190 mm  [stored 3.9042 ft]; Intruderprufe LowE SHGC Value=0.516; Intruderprufe LowE U Value=4.96; Intruderprufe SHGC Value=0.582; Intruderprufe U Value=6.46; Is Heavy Duty Interlocker=0 mm  [stored 0 ft]; Limit Sash Width Left Max=1200 mm; Limit Sash Width Left Min=872 mm; Max Pane Area=0.93 m²; Sash Height=1110 mm; Sash Width Left=1036 mm; Sash Width Right=1036 mm; Standard Interlocker=Yes; Width=2090 mm  [stored 6.85696 ft]; Windload Design=1500 mm  [stored 4.92126 ft]
- 540SW-2112XX-2000Pa: Area Left Sash Glazing=0.93 m²; Area Right Sash Glazing=0.93 m²; Clearvue SHGC Value=0.617; Clearvue U Value=6.57; Custom Windload=2000 mm  [stored 6.56168 ft]; Custom Window Height=1190 mm  [stored 3.9042 ft]; Custom Window Width=2090 mm  [stored 6.85696 ft]; Energy Advantage SHGC Value=0.554; Energy Advantage U Value=5.05; Heavy Duty Interlocker=Yes; Height=1190 mm  [stored 3.9042 ft]; Intruderprufe LowE SHGC Value=0.516; Intruderprufe LowE U Value=4.96; Intruderprufe SHGC Value=0.582; Intruderprufe U Value=6.46; Is Heavy Duty Interlocker=1 mm  [stored 0.00328084 ft]; Limit Sash Width Left Max=1200 mm; Limit Sash Width Left Min=872 mm; Max Pane Area=0.93 m²; Sash Height=1110 mm; Sash Width Left=1036 mm; Sash Width Right=1036 mm; Standard Interlocker=No; Width=2090 mm  [stored 6.85696 ft]; Windload Design=2000 mm  [stored 6.56168 ft]
- 540SW-2115XX-1500Pa: Area Left Sash Glazing=1.21 m²; Area Right Sash Glazing=1.21 m²; Clearvue SHGC Value=0.642; Clearvue U Value=6.52; Custom Windload=1500 mm  [stored 4.92126 ft]; Custom Window Height=1490 mm  [stored 4.88845 ft]; Custom Window Width=2090 mm  [stored 6.85696 ft]; Energy Advantage SHGC Value=0.576; Energy Advantage U Value=4.93; Heavy Duty Interlocker=Yes; Height=1490 mm  [stored 4.88845 ft]; Intruderprufe LowE SHGC Value=0.536; Intruderprufe LowE U Value=4.84; Intruderprufe SHGC Value=0.606; Intruderprufe U Value=6.4; Is Heavy Duty Interlocker=1 mm  [stored 0.00328084 ft]; Limit Sash Width Left Max=1200 mm; Limit Sash Width Left Min=872 mm; Max Pane Area=1.21 m²; Sash Height=1410 mm; Sash Width Left=1036 mm; Sash Width Right=1036 mm; Standard Interlocker=No; Width=2090 mm  [stored 6.85696 ft]; Windload Design=1500 mm  [stored 4.92126 ft]
- 540SW-2115XX-2000Pa: Area Left Sash Glazing=1.21 m²; Area Right Sash Glazing=1.21 m²; Clearvue SHGC Value=0.642; Clearvue U Value=6.52; Custom Windload=2000 mm  [stored 6.56168 ft]; Custom Window Height=1490 mm  [stored 4.88845 ft]; Custom Window Width=2090 mm  [stored 6.85696 ft]; Energy Advantage SHGC Value=0.576; Energy Advantage U Value=4.93; Heavy Duty Interlocker=Yes; Height=1490 mm  [stored 4.88845 ft]; Intruderprufe LowE SHGC Value=0.536; Intruderprufe LowE U Value=4.84; Intruderprufe SHGC Value=0.606; Intruderprufe U Value=6.4; Is Heavy Duty Interlocker=1 mm  [stored 0.00328084 ft]; Limit Sash Width Left Max=1200 mm; Limit Sash Width Left Min=872 mm; Max Pane Area=1.21 m²; Sash Height=1410 mm; Sash Width Left=1036 mm; Sash Width Right=1036 mm; Standard Interlocker=No; Width=2090 mm  [stored 6.85696 ft]; Windload Design=2000 mm  [stored 6.56168 ft]
- 540SW-2406XX-1500Pa: Area Left Sash Glazing=0.43 m²; Area Right Sash Glazing=0.43 m²; Clearvue SHGC Value=0.501; Clearvue U Value=6.8; Custom Windload=1500 mm  [stored 4.92126 ft]; Custom Window Height=590 mm  [stored 1.9357 ft]; Custom Window Width=2390 mm  [stored 7.84121 ft]; Energy Advantage SHGC Value=0.451; Energy Advantage U Value=5.61; Heavy Duty Interlocker=No; Height=590 mm  [stored 1.9357 ft]; Intruderprufe LowE SHGC Value=0.421; Intruderprufe LowE U Value=5.51; Intruderprufe SHGC Value=0.473; Intruderprufe U Value=6.69; Is Heavy Duty Interlocker=0 mm  [stored 0 ft]; Limit Sash Width Left Max=1200 mm; Limit Sash Width Left Min=1172 mm; Max Pane Area=0.43 m²; Sash Height=510 mm; Sash Width Left=1186 mm; Sash Width Right=1186 mm; Standard Interlocker=Yes; Width=2390 mm  [stored 7.84121 ft]; Windload Design=1500 mm  [stored 4.92126 ft]
- 540SW-2406XX-2000Pa: Area Left Sash Glazing=0.43 m²; Area Right Sash Glazing=0.43 m²; Clearvue SHGC Value=0.501; Clearvue U Value=6.8; Custom Windload=2000 mm  [stored 6.56168 ft]; Custom Window Height=590 mm  [stored 1.9357 ft]; Custom Window Width=2390 mm  [stored 7.84121 ft]; Energy Advantage SHGC Value=0.451; Energy Advantage U Value=5.61; Heavy Duty Interlocker=No; Height=590 mm  [stored 1.9357 ft]; Intruderprufe LowE SHGC Value=0.421; Intruderprufe LowE U Value=5.51; Intruderprufe SHGC Value=0.473; Intruderprufe U Value=6.69; Is Heavy Duty Interlocker=0 mm  [stored 0 ft]; Limit Sash Width Left Max=1200 mm; Limit Sash Width Left Min=1172 mm; Max Pane Area=0.43 m²; Sash Height=510 mm; Sash Width Left=1186 mm; Sash Width Right=1186 mm; Standard Interlocker=Yes; Width=2390 mm  [stored 7.84121 ft]; Windload Design=2000 mm  [stored 6.56168 ft]
- 540SW-2409XX-1500Pa: Area Left Sash Glazing=0.76 m²; Area Right Sash Glazing=0.76 m²; Clearvue SHGC Value=0.586; Clearvue U Value=6.62; Custom Windload=1500 mm  [stored 4.92126 ft]; Custom Window Height=890 mm  [stored 2.91995 ft]; Custom Window Width=2390 mm  [stored 7.84121 ft]; Energy Advantage SHGC Value=0.526; Energy Advantage U Value=5.19; Heavy Duty Interlocker=No; Height=890 mm  [stored 2.91995 ft]; Intruderprufe LowE SHGC Value=0.491; Intruderprufe LowE U Value=5.09; Intruderprufe SHGC Value=0.553; Intruderprufe U Value=6.5; Is Heavy Duty Interlocker=0 mm  [stored 0 ft]; Limit Sash Width Left Max=1200 mm; Limit Sash Width Left Min=1172 mm; Max Pane Area=0.76 m²; Sash Height=810 mm; Sash Width Left=1186 mm; Sash Width Right=1186 mm; Standard Interlocker=Yes; Width=2390 mm  [stored 7.84121 ft]; Windload Design=1500 mm  [stored 4.92126 ft]
- 540SW-2409XX-2000Pa: Area Left Sash Glazing=0.76 m²; Area Right Sash Glazing=0.76 m²; Clearvue SHGC Value=0.586; Clearvue U Value=6.62; Custom Windload=2000 mm  [stored 6.56168 ft]; Custom Window Height=890 mm  [stored 2.91995 ft]; Custom Window Width=2390 mm  [stored 7.84121 ft]; Energy Advantage SHGC Value=0.526; Energy Advantage U Value=5.19; Heavy Duty Interlocker=No; Height=890 mm  [stored 2.91995 ft]; Intruderprufe LowE SHGC Value=0.491; Intruderprufe LowE U Value=5.09; Intruderprufe SHGC Value=0.553; Intruderprufe U Value=6.5; Is Heavy Duty Interlocker=0 mm  [stored 0 ft]; Limit Sash Width Left Max=1200 mm; Limit Sash Width Left Min=1172 mm; Max Pane Area=0.76 m²; Sash Height=810 mm; Sash Width Left=1186 mm; Sash Width Right=1186 mm; Standard Interlocker=Yes; Width=2390 mm  [stored 7.84121 ft]; Windload Design=2000 mm  [stored 6.56168 ft]
- 540SW-2412XX-1500Pa: Area Left Sash Glazing=1.08 m²; Area Right Sash Glazing=1.08 m²; Clearvue SHGC Value=0.629; Clearvue U Value=6.53; Custom Windload=1500 mm  [stored 4.92126 ft]; Custom Window Height=1190 mm  [stored 3.9042 ft]; Custom Window Width=2390 mm  [stored 7.84121 ft]; Energy Advantage SHGC Value=0.564; Energy Advantage U Value=4.98; Heavy Duty Interlocker=No; Height=1190 mm  [stored 3.9042 ft]; Intruderprufe LowE SHGC Value=0.525; Intruderprufe LowE U Value=4.89; Intruderprufe SHGC Value=0.593; Intruderprufe U Value=6.41; Is Heavy Duty Interlocker=0 mm  [stored 0 ft]; Limit Sash Width Left Max=1200 mm; Limit Sash Width Left Min=1172 mm; Max Pane Area=1.08 m²; Sash Height=1110 mm; Sash Width Left=1186 mm; Sash Width Right=1186 mm; Standard Interlocker=Yes; Width=2390 mm  [stored 7.84121 ft]; Windload Design=1500 mm  [stored 4.92126 ft]
- 540SW-2412XX-2000Pa: Area Left Sash Glazing=1.08 m²; Area Right Sash Glazing=1.08 m²; Clearvue SHGC Value=0.629; Clearvue U Value=6.53; Custom Windload=2000 mm  [stored 6.56168 ft]; Custom Window Height=1190 mm  [stored 3.9042 ft]; Custom Window Width=2390 mm  [stored 7.84121 ft]; Energy Advantage SHGC Value=0.564; Energy Advantage U Value=4.98; Heavy Duty Interlocker=Yes; Height=1190 mm  [stored 3.9042 ft]; Intruderprufe LowE SHGC Value=0.525; Intruderprufe LowE U Value=4.89; Intruderprufe SHGC Value=0.593; Intruderprufe U Value=6.41; Is Heavy Duty Interlocker=1 mm  [stored 0.00328084 ft]; Limit Sash Width Left Max=1200 mm; Limit Sash Width Left Min=1172 mm; Max Pane Area=1.08 m²; Sash Height=1110 mm; Sash Width Left=1186 mm; Sash Width Right=1186 mm; Standard Interlocker=No; Width=2390 mm  [stored 7.84121 ft]; Windload Design=2000 mm  [stored 6.56168 ft]
- 540SW-2415XX-1500Pa: Area Left Sash Glazing=1.4 m²; Area Right Sash Glazing=1.4 m²; Clearvue SHGC Value=0.654; Clearvue U Value=6.48; Custom Windload=1500 mm  [stored 4.92126 ft]; Custom Window Height=1490 mm  [stored 4.88845 ft]; Custom Window Width=2390 mm  [stored 7.84121 ft]; Energy Advantage SHGC Value=0.586; Energy Advantage U Value=4.85; Heavy Duty Interlocker=Yes; Height=1490 mm  [stored 4.88845 ft]; Intruderprufe LowE SHGC Value=0.546; Intruderprufe LowE U Value=4.77; Intruderprufe SHGC Value=0.617; Intruderprufe U Value=6.36; Is Heavy Duty Interlocker=1 mm  [stored 0.00328084 ft]; Limit Sash Width Left Max=1200 mm; Limit Sash Width Left Min=1172 mm; Max Pane Area=1.4 m²; Sash Height=1410 mm; Sash Width Left=1186 mm; Sash Width Right=1186 mm; Standard Interlocker=No; Width=2390 mm  [stored 7.84121 ft]; Windload Design=1500 mm  [stored 4.92126 ft]
- 540SW-2415XX-2000Pa: Area Left Sash Glazing=1.4 m²; Area Right Sash Glazing=1.4 m²; Clearvue SHGC Value=0.654; Clearvue U Value=6.48; Custom Windload=2000 mm  [stored 6.56168 ft]; Custom Window Height=1490 mm  [stored 4.88845 ft]; Custom Window Width=2390 mm  [stored 7.84121 ft]; Energy Advantage SHGC Value=0.586; Energy Advantage U Value=4.85; Heavy Duty Interlocker=Yes; Height=1490 mm  [stored 4.88845 ft]; Intruderprufe LowE SHGC Value=0.546; Intruderprufe LowE U Value=4.77; Intruderprufe SHGC Value=0.617; Intruderprufe U Value=6.36; Is Heavy Duty Interlocker=1 mm  [stored 0.00328084 ft]; Limit Sash Width Left Max=1200 mm; Limit Sash Width Left Min=1172 mm; Max Pane Area=1.4 m²; Sash Height=1410 mm; Sash Width Left=1186 mm; Sash Width Right=1186 mm; Standard Interlocker=No; Width=2390 mm  [stored 7.84121 ft]; Windload Design=2000 mm  [stored 6.56168 ft]

note: [stored X ft] marks values corroborated as IEEE doubles in the binary element streams (Revit-internal decimal feet)

## geometry (parser evidence)
native form markers: Sweep x9
no freeform markers — native parametric forms only
